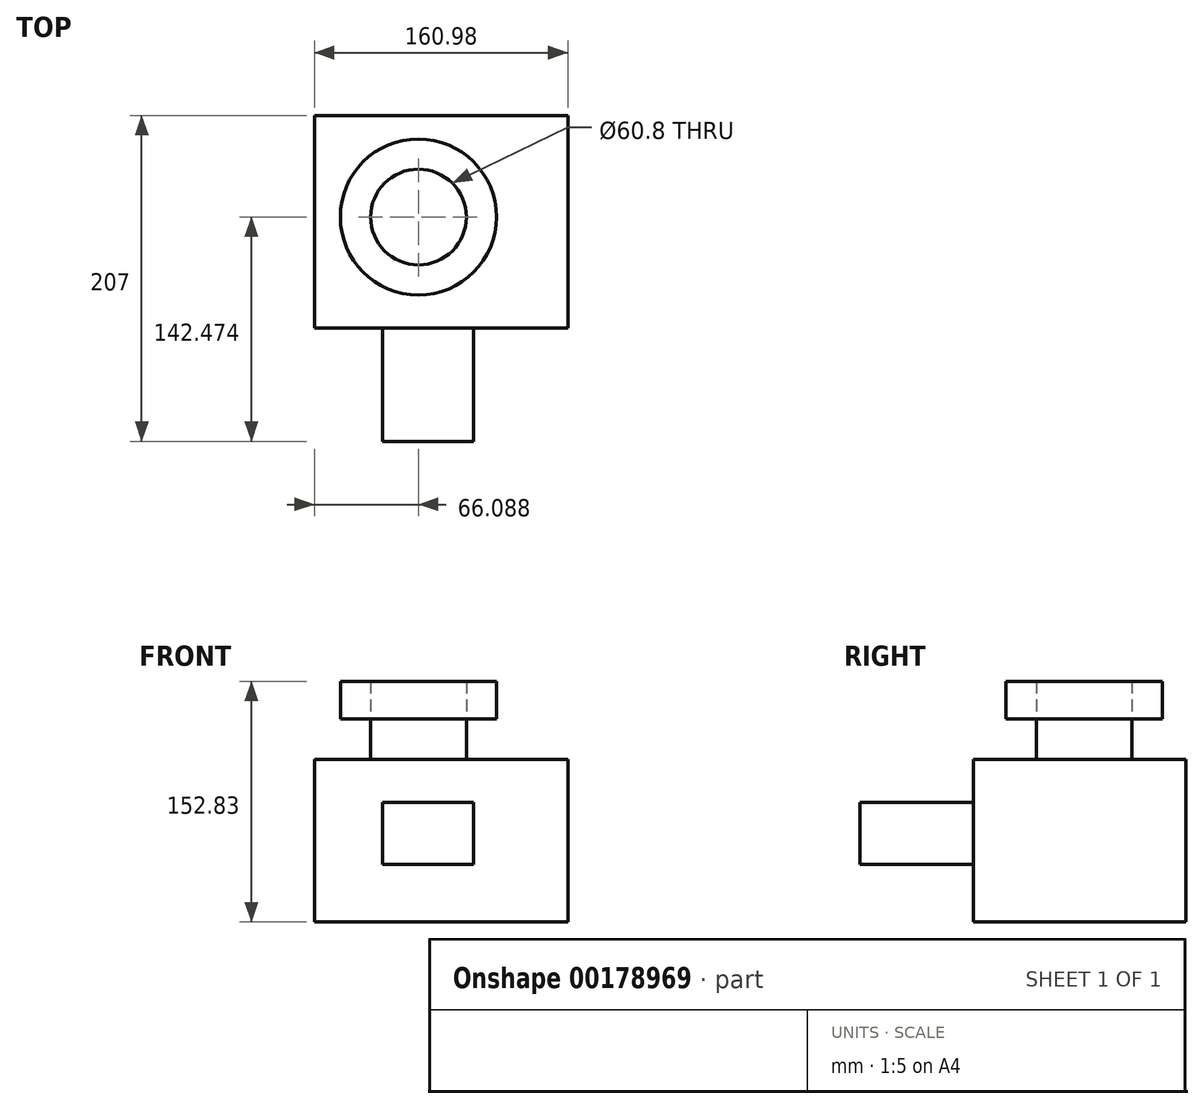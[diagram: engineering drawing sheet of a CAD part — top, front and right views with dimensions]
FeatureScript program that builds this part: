
annotation { "Feature Type Name" : "Feature", "Feature Type Description" : "" }
export const myFeature = defineFeature(function(context is Context, id is Id, definition is map)
    precondition{}
    {
        {
            var Q0;
            Q0=qCreatedBy(makeId("Front.planeOp"),FACE);
            var sketch = newSketch(context, id + "F0", { "sketchPlane" : qUnion([Q0])});
            skLineSegment(sketch, "E0.bottom", {"start": v(-100.99, 66.91) * mm, "end": v(59.99, 66.91) * mm});
            skLineSegment(sketch, "E0.top", {"start": v(-100.99, -36.52) * mm, "end": v(59.99, -36.52) * mm});
            skLineSegment(sketch, "E0.left", {"start": v(-100.99, 66.91) * mm, "end": v(-100.99, -36.52) * mm});
            skLineSegment(sketch, "E0.right", {"start": v(59.99, 66.91) * mm, "end": v(59.99, -36.52) * mm});
            skLineSegment(sketch, "E1", {"start": v(59.99, 15.2) * mm, "end": v(149.52, 38.97) * mm});
            skLineSegment(sketch, "E2", {"start": v(149.52, 38.97) * mm, "end": v(59.99, 66.91) * mm});
            skSolve(sketch);
        }
        {
            var Q0;
            {var subQ1=sQuery(id+"F0.wireOp",EDGE,"E0.bottom");Q0=makeQuery(id+"F0.imprint","IMPRINT",FACE,{"disambiguationData":[TD([[makeQuery(id+"F0.imprint","IMPRINT",EDGE,{"derivedFrom":subQ1}),-1.0]])]});}
            extrude(context, id + "F1", {"entities" : qUnion([Q0]), "depth" : 135 * mm});
        }
        {
            var Q0;
            Q0=makeQuery(id+"F1.opExtrude","CAP_FACE",FACE,{"disambiguationData":[OSD([sQuery(id+"F0.wireOp",EDGE,"E0.bottom"),sQuery(id+"F0.wireOp",EDGE,"E0.top"),sQuery(id+"F0.wireOp",EDGE,"E0.left"),sQuery(id+"F0.wireOp",EDGE,"E0.right")])],"isStart":false});
            var sketch = newSketch(context, id + "F2", { "sketchPlane" : qUnion([Q0])});
            skLineSegment(sketch, "E3.bottom", {"start": v(-57.67, 39.43) * mm, "end": v(0, 39.43) * mm});
            skLineSegment(sketch, "E3.top", {"start": v(-57.67, 0) * mm, "end": v(0, 0) * mm});
            skLineSegment(sketch, "E3.left", {"start": v(-57.67, 39.43) * mm, "end": v(-57.67, 0) * mm});
            skLineSegment(sketch, "E3.right", {"start": v(0, 39.43) * mm, "end": v(0, 0) * mm});
            skSolve(sketch);
        }
        {
            var Q0;
            Q0=makeQuery(id+"F2.imprint","IMPRINT",FACE,{"disambiguationData":[TD([[makeQuery(id+"F2.imprint","IMPRINT",EDGE,{"derivedFrom":sQuery(id+"F2.wireOp",EDGE,"E3.bottom")}),-1.0]])]});
            extrude(context, id + "F3", {"entities" : qUnion([Q0]), "depth" : 72 * mm});
        }
        {
            var Q0;
            Q0=makeQuery(id+"F1.opExtrude","SWEPT_FACE",FACE,{"disambiguationData":[OSD([sQuery(id+"F0.wireOp",EDGE,"E0.bottom")])]});
            var sketch = newSketch(context, id + "F4", { "sketchPlane" : qUnion([Q0])});
            skCircle(sketch, "E4", {"center": v(-34.9, -64.53) * mm, "radius": 30.4 * mm});
            skSolve(sketch);
        }
        {
            var Q0;
            Q0=makeQuery(id+"F4.imprint","IMPRINT",FACE,{"disambiguationData":[TD([[makeQuery(id+"F4.imprint","IMPRINT",EDGE,{"derivedFrom":sQuery(id+"F4.wireOp",EDGE,"E4")}),1.0]])]});
            extrude(context, id + "F5", {"entities" : qUnion([Q0]), "depth" : 49.4 * mm});
        }
        {
            var Q0;
            Q0=makeQuery(id+"F5.opExtrude","CAP_FACE",FACE,{"disambiguationData":[OSD([sQuery(id+"F4.wireOp",EDGE,"E4")])],"isStart":false});
            var sketch = newSketch(context, id + "F6", { "sketchPlane" : qUnion([Q0])});
            skCircle(sketch, "E5", {"center": v(-34.9, -64.53) * mm, "radius": 49.6 * mm});
            skSolve(sketch);
        }
        {
            var Q0;
            Q0=makeQuery(id+"F6.imprint","IMPRINT",FACE,{"disambiguationData":[TD([[makeQuery(id+"F6.imprint","IMPRINT",EDGE,{"derivedFrom":sQuery(id+"F6.wireOp",EDGE,"E5")}),1.0]])]});
            extrude(context, id + "F7", {"entities" : qUnion([Q0]), "oppositeDirection" : true, "depth" : 23.9 * mm});
        }
    });
